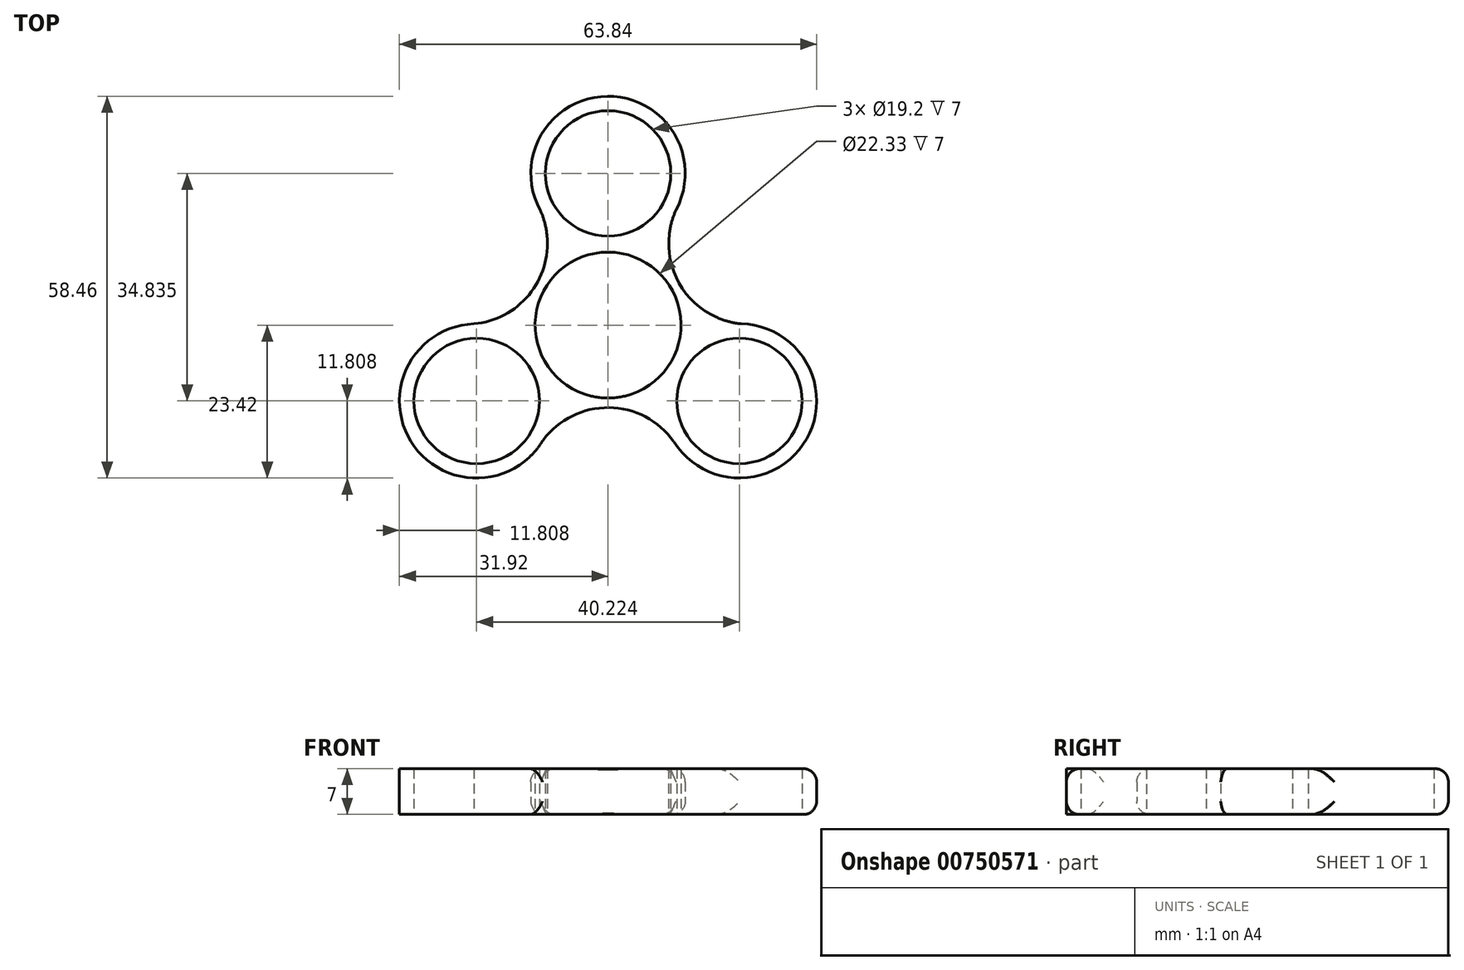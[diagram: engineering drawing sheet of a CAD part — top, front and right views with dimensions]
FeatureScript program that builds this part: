
annotation { "Feature Type Name" : "Feature", "Feature Type Description" : "" }
export const myFeature = defineFeature(function(context is Context, id is Id, definition is map)
    precondition{}
    {
        {
            var Q0;
            Q0=qCreatedBy(makeId("Top.planeOp"),FACE);
            var sketch = newSketch(context, id + "F0", { "sketchPlane" : qUnion([Q0])});
            skCircle(sketch, "E0", {"center": v(0, 0) * mm, "radius": 11.16 * mm});
            skCircle(sketch, "E1", {"center": v(0, 0) * mm, "radius": 13.1 * mm});
            skCircle(sketch, "E2", {"center": v(0, 23.22) * mm, "radius": 9.6 * mm});
            skCircle(sketch, "E3", {"center": v(0, 23.22) * mm, "radius": 11.81 * mm});
            skCircle(sketch, "E4.1.0", {"center": v(-20.11, -11.61) * mm, "radius": 9.6 * mm});
            skCircle(sketch, "E4.1.1", {"center": v(-20.11, -11.61) * mm, "radius": 11.81 * mm});
            skCircle(sketch, "E4.2.0", {"center": v(20.11, -11.61) * mm, "radius": 9.6 * mm});
            skCircle(sketch, "E4.2.1", {"center": v(20.11, -11.61) * mm, "radius": 11.81 * mm});
            skArc(sketch, "E5", {"start": v(-20.5, 0.2) * mm, "mid": v(-10.99, 6.23) * mm, "end": v(-10.32, 17.47) * mm});
            skArc(sketch, "E6.1.0", {"start": v(10.09, -17.86) * mm, "mid": v(0.1, -12.63) * mm, "end": v(-9.97, -17.67) * mm});
            skArc(sketch, "E6.2.0", {"start": v(10.42, 17.66) * mm, "mid": v(10.89, 6.4) * mm, "end": v(20.3, 0.2) * mm});
            skSolve(sketch);
        }
        {
            var Q0;
            Q0=makeQuery(id+"F0.imprint","IMPRINT",FACE,{"disambiguationData":[TD([[makeQuery(id+"F0.imprint","IMPRINT",EDGE,{"derivedFrom":sQuery(id+"F0.wireOp",EDGE,"E0")}),-1.0]])]});
            var Q1;
            Q1=makeQuery(id+"F0.imprint","IMPRINT",FACE,{"disambiguationData":[TD([[makeQuery(id+"F0.imprint","IMPRINT",EDGE,{"derivedFrom":sQuery(id+"F0.wireOp",EDGE,"E4.1.0")}),-1.0]])]});
            var Q2;
            Q2=makeQuery(id+"F0.imprint","IMPRINT",FACE,{"disambiguationData":[TD([[makeQuery(id+"F0.imprint","IMPRINT",EDGE,{"derivedFrom":sQuery(id+"F0.wireOp",EDGE,"E4.2.0")}),-1.0]])]});
            var Q3;
            {var subQ0=sQuery(id+"F0.wireOp",EDGE,"E3");var subQ1=sQuery(id+"F0.wireOp",EDGE,"E1");var subQ2=makeQuery(id+"F0.imprint","INTERSECT",VERTEX,{"disambiguationData":[OD(0.0)],"derivedFrom":[subQ1,subQ0]});Q3=makeQuery(id+"F0.imprint","IMPRINT",FACE,{"disambiguationData":[TD([[makeQuery(id+"F0.imprint","IMPRINT",EDGE,{"disambiguationData":[TD([[subQ2,1.0]])],"derivedFrom":subQ1}),1.0]])]});}
            var Q4;
            {var subQ0=sQuery(id+"F0.wireOp",EDGE,"E4.1.1");var subQ1=sQuery(id+"F0.wireOp",EDGE,"E1");var subQ2=makeQuery(id+"F0.imprint","INTERSECT",VERTEX,{"disambiguationData":[OD(0.0)],"derivedFrom":[subQ1,subQ0]});Q4=makeQuery(id+"F0.imprint","IMPRINT",FACE,{"disambiguationData":[TD([[makeQuery(id+"F0.imprint","IMPRINT",EDGE,{"disambiguationData":[TD([[subQ2,-1.0]])],"derivedFrom":subQ1}),1.0]])]});}
            var Q5;
            {var subQ0=sQuery(id+"F0.wireOp",EDGE,"E4.2.1");var subQ1=sQuery(id+"F0.wireOp",EDGE,"E1");var subQ2=makeQuery(id+"F0.imprint","INTERSECT",VERTEX,{"disambiguationData":[OD(0.0)],"derivedFrom":[subQ1,subQ0]});Q5=makeQuery(id+"F0.imprint","IMPRINT",FACE,{"disambiguationData":[TD([[makeQuery(id+"F0.imprint","IMPRINT",EDGE,{"disambiguationData":[TD([[subQ2,-1.0]])],"derivedFrom":subQ1}),1.0]])]});}
            var Q6;
            Q6=makeQuery(id+"F0.imprint","IMPRINT",FACE,{"disambiguationData":[TD([[makeQuery(id+"F0.imprint","IMPRINT",EDGE,{"derivedFrom":sQuery(id+"F0.wireOp",EDGE,"E2")}),-1.0]])]});
            var Q7;
            {var subQ0=sQuery(id+"F0.wireOp",EDGE,"E3");var subQ1=sQuery(id+"F0.wireOp",EDGE,"E1");var subQ2=makeQuery(id+"F0.imprint","INTERSECT",VERTEX,{"disambiguationData":[OD(0.0)],"derivedFrom":[subQ1,subQ0]});Q7=makeQuery(id+"F0.imprint","IMPRINT",FACE,{"disambiguationData":[TD([[makeQuery(id+"F0.imprint","IMPRINT",EDGE,{"disambiguationData":[TD([[subQ2,-1.0]])],"derivedFrom":subQ1}),1.0]])]});}
            var Q8;
            {var subQ0=sQuery(id+"F0.wireOp",EDGE,"E5");var subQ1=sQuery(id+"F0.wireOp",EDGE,"E1");var subQ2=makeQuery(id+"F0.imprint","INTERSECT",VERTEX,{"disambiguationData":[OD(0.0)],"derivedFrom":[subQ1,subQ0]});Q8=makeQuery(id+"F0.imprint","IMPRINT",FACE,{"disambiguationData":[TD([[makeQuery(id+"F0.imprint","IMPRINT",EDGE,{"disambiguationData":[TD([[subQ2,1.0]])],"derivedFrom":subQ1}),-1.0]])]});}
            var Q9;
            {var subQ0=sQuery(id+"F0.wireOp",EDGE,"E6.2.0");var subQ1=sQuery(id+"F0.wireOp",EDGE,"E1");var subQ2=makeQuery(id+"F0.imprint","INTERSECT",VERTEX,{"disambiguationData":[OD(0.0)],"derivedFrom":[subQ1,subQ0]});Q9=makeQuery(id+"F0.imprint","IMPRINT",FACE,{"disambiguationData":[TD([[makeQuery(id+"F0.imprint","IMPRINT",EDGE,{"disambiguationData":[TD([[subQ2,-1.0]])],"derivedFrom":subQ1}),-1.0]])]});}
            var Q10;
            {var subQ0=sQuery(id+"F0.wireOp",EDGE,"E6.2.0");var subQ1=sQuery(id+"F0.wireOp",EDGE,"E1");var subQ2=makeQuery(id+"F0.imprint","INTERSECT",VERTEX,{"disambiguationData":[OD(1.0)],"derivedFrom":[subQ1,subQ0]});Q10=makeQuery(id+"F0.imprint","IMPRINT",FACE,{"disambiguationData":[TD([[makeQuery(id+"F0.imprint","IMPRINT",EDGE,{"disambiguationData":[TD([[subQ2,1.0]])],"derivedFrom":subQ1}),-1.0]])]});}
            var Q11;
            {var subQ0=sQuery(id+"F0.wireOp",EDGE,"E5");var subQ1=sQuery(id+"F0.wireOp",EDGE,"E1");var subQ2=makeQuery(id+"F0.imprint","INTERSECT",VERTEX,{"disambiguationData":[OD(1.0)],"derivedFrom":[subQ1,subQ0]});Q11=makeQuery(id+"F0.imprint","IMPRINT",FACE,{"disambiguationData":[TD([[makeQuery(id+"F0.imprint","IMPRINT",EDGE,{"disambiguationData":[TD([[subQ2,-1.0]])],"derivedFrom":subQ1}),-1.0]])]});}
            var Q12;
            {var subQ0=sQuery(id+"F0.wireOp",EDGE,"E6.1.0");var subQ1=sQuery(id+"F0.wireOp",EDGE,"E1");var subQ2=makeQuery(id+"F0.imprint","INTERSECT",VERTEX,{"disambiguationData":[OD(0.0)],"derivedFrom":[subQ1,subQ0]});Q12=makeQuery(id+"F0.imprint","IMPRINT",FACE,{"disambiguationData":[TD([[makeQuery(id+"F0.imprint","IMPRINT",EDGE,{"disambiguationData":[TD([[subQ2,1.0]])],"derivedFrom":subQ1}),-1.0]])]});}
            var Q13;
            {var subQ0=sQuery(id+"F0.wireOp",EDGE,"E6.1.0");var subQ1=sQuery(id+"F0.wireOp",EDGE,"E1");var subQ2=makeQuery(id+"F0.imprint","INTERSECT",VERTEX,{"disambiguationData":[OD(1.0)],"derivedFrom":[subQ1,subQ0]});Q13=makeQuery(id+"F0.imprint","IMPRINT",FACE,{"disambiguationData":[TD([[makeQuery(id+"F0.imprint","IMPRINT",EDGE,{"disambiguationData":[TD([[subQ2,-1.0]])],"derivedFrom":subQ1}),-1.0]])]});}
            extrude(context, id + "F1", {"entities" : qUnion([Q0, Q1, Q2, Q3, Q4, Q5, Q6, Q7, Q8, Q9, Q10, Q11, Q12, Q13]), "depth" : 7 * mm, "offsetDistance" : 25 * mm});
        }
        {
            var Q0;
            Q0=makeQuery(id+"F1.opExtrude","SWEPT_FACE",FACE,{"disambiguationData":[OSD([sQuery(id+"F0.wireOp",EDGE,"E6.1.0")])]});
            var Q1;
            Q1=makeQuery(id+"F1.opExtrude","SWEPT_FACE",FACE,{"disambiguationData":[OSD([sQuery(id+"F0.wireOp",EDGE,"E4.2.1")])]});
            var Q2;
            Q2=makeQuery(id+"F1.opExtrude","SWEPT_FACE",FACE,{"disambiguationData":[OSD([sQuery(id+"F0.wireOp",EDGE,"E3")])]});
            fillet(context, id + "F2", {"entities" : qUnion([Q0, Q1, Q2]), "radius" : 2 * mm, "tangentPropagation" : true, "allowEdgeOverflow" : false});
        }
    });
